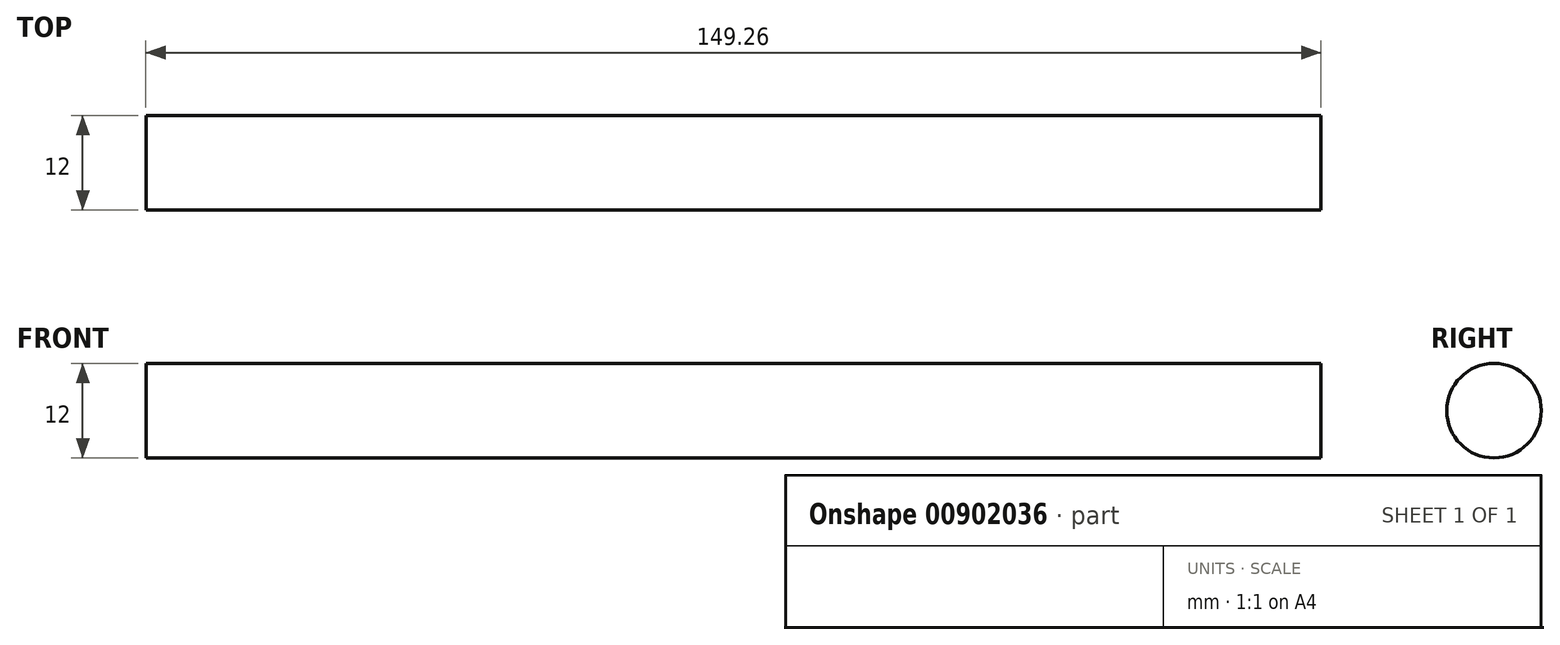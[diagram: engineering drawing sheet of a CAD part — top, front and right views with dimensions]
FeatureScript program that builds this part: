
annotation { "Feature Type Name" : "Feature", "Feature Type Description" : "" }
export const myFeature = defineFeature(function(context is Context, id is Id, definition is map)
    precondition{}
    {
        {
            var Q0;
            Q0=qCreatedBy(makeId("Right.planeOp"),FACE);
            var sketch = newSketch(context, id + "F0", { "sketchPlane" : qUnion([Q0])});
            skCircle(sketch, "E0", {"center": v(-27.46, 15.67) * mm, "radius": 6 * mm});
            skSolve(sketch);
        }
        {
            var Q0;
            Q0=makeQuery(id+"F0.imprint","IMPRINT",FACE,{"disambiguationData":[TD([[makeQuery(id+"F0.imprint","IMPRINT",EDGE,{"derivedFrom":sQuery(id+"F0.wireOp",EDGE,"E0")}),1.0]])]});
            extrude(context, id + "F1", {"entities" : qUnion([Q0]), "endBound" : BoundingType.SYMMETRIC, "depth" : 149.25 * mm, "offsetDistance" : 25 * mm});
        }
    });
